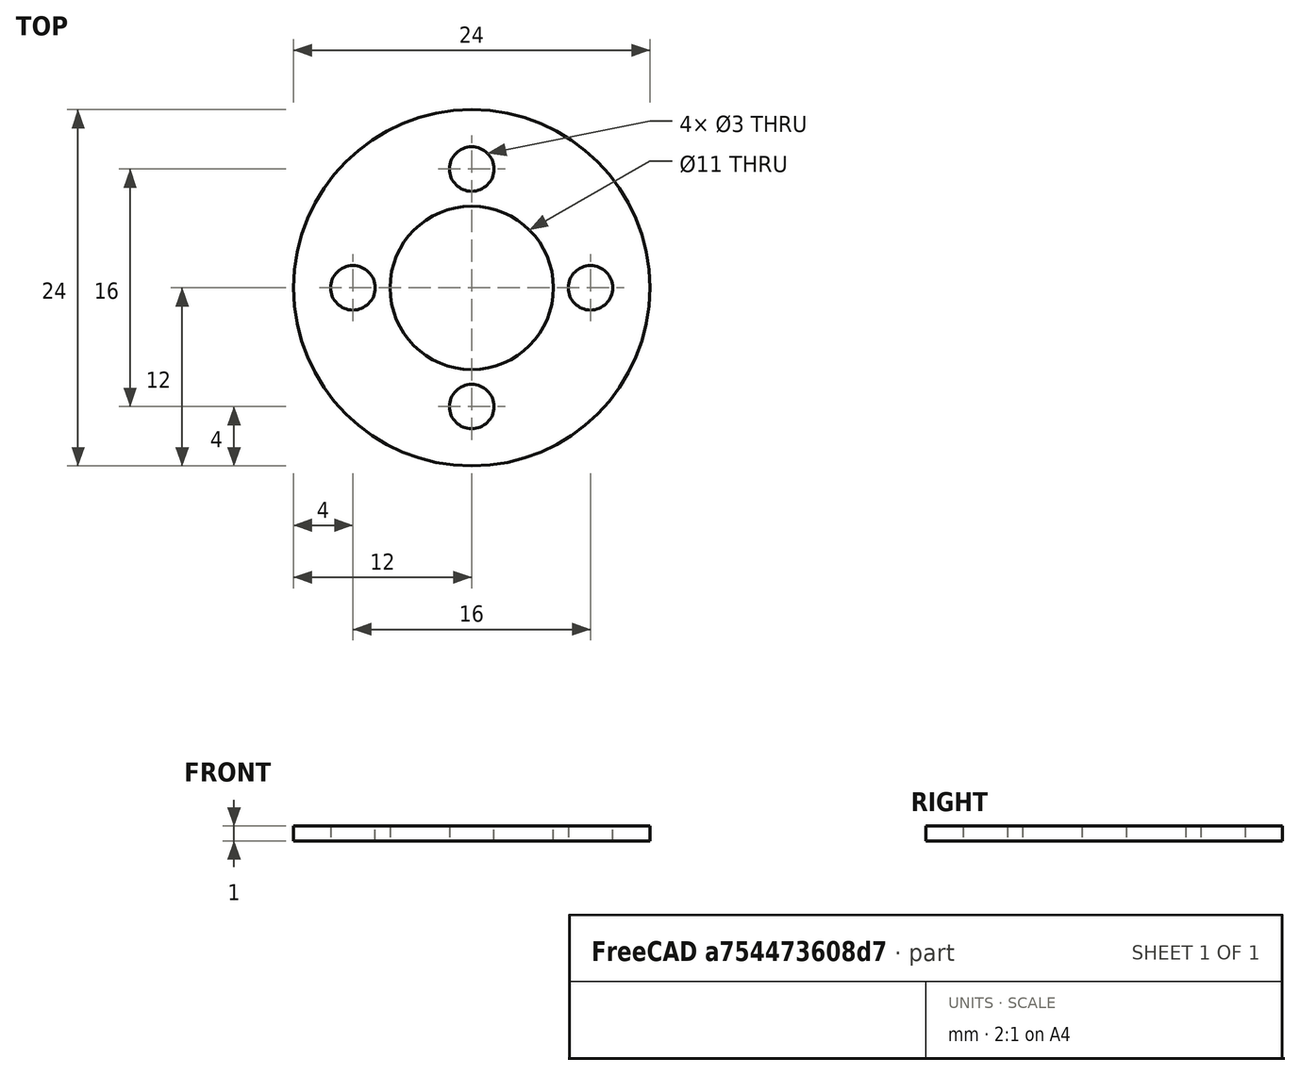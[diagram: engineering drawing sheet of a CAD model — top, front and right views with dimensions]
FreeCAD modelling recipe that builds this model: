
FCSTD DOCUMENT  (FreeCAD 0.19R)
Label: rondelle_ecrasement_caoutchouc
License: All rights reserved
LicenseURL: http://en.wikipedia.org/wiki/All_rights_reserved
objects: Sketcher::SketchObject×1, PartDesign::Pad×1, PartDesign::Body×1
note: 4 computed .brp shape members not serialized (recipe doc carries the construction recipe); baked Part::Feature solids carry a one-line shape summary decoded from their .brp

FEATURE [Sketcher::SketchObject] Sketch
  FullyConstrained = true
  MapMode = 5
  Support = -> [XY_Plane]
  sketch-geometry (6):
    g0: Circle CenterX=0 CenterY=0 CenterZ=0 NormalX=0 NormalY=0 NormalZ=1 AngleXU=0 Radius=12
    g1: Circle CenterX=0 CenterY=8 CenterZ=0 NormalX=0 NormalY=0 NormalZ=1 AngleXU=0 Radius=1.5
    g2: Circle CenterX=-8 CenterY=0 CenterZ=0 NormalX=0 NormalY=0 NormalZ=1 AngleXU=0 Radius=1.5
    g3: Circle CenterX=0 CenterY=-8 CenterZ=0 NormalX=0 NormalY=0 NormalZ=1 AngleXU=0 Radius=1.5
    g4: Circle CenterX=8 CenterY=0 CenterZ=0 NormalX=0 NormalY=0 NormalZ=1 AngleXU=0 Radius=1.5
    g5: Circle CenterX=0 CenterY=0 CenterZ=0 NormalX=0 NormalY=0 NormalZ=1 AngleXU=0 Radius=5.5
  constraints (16):
    c: Coincident(g0,g-1)
    c: Radius(g0) = 12
    c: PointOnObject(g1,g-2)
    c: PointOnObject(g2,g-1)
    c: PointOnObject(g3,g-2)
    c: PointOnObject(g4,g-1)
    c: Radius(g1) = 1.5
    c: Radius(g2) = 1.5
    c: Radius(g3) = 1.5
    c: Radius(g4) = 1.5
    c: DistanceY(g0,g1) = 8
    c: DistanceY(g3,g0) = 8
    c: DistanceX(g2,g0) = 8
    c: DistanceX(g0,g4) = 8
    c: Coincident(g5,g0)
    c: Radius(g5) = 5.5
FEATURE [PartDesign::Pad] Pad
  Direction = (1,1,1)
  Length = 1
  Length2 = 100
  Profile = -> Sketch
  Type = 0
FEATURE [PartDesign::Body] Body
  Group = -> [Sketch,Pad]
  Origin = -> Origin
  Tip = -> Pad
